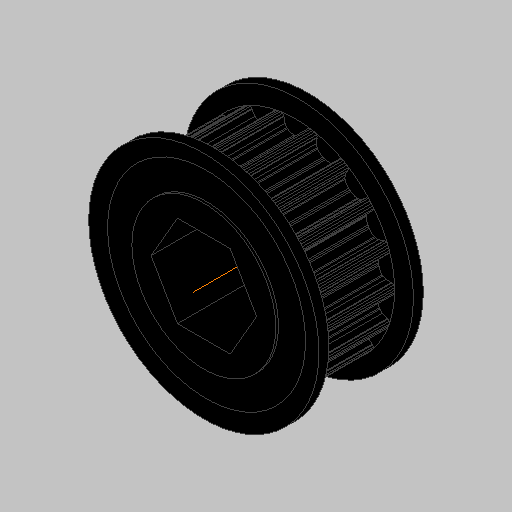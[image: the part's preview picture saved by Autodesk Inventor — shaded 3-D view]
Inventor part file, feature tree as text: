
AUTODESK INVENTOR PART (.ipt)
format: ipt  version: 2023.5 (Build 275446000, 446)  size: 594,944 bytes
history: native  units: in
note: dims shown in document units (in); Inventor stores cm internally (conversion verified against a paired STEP export)
features: plane x1, mirror x1
ambient origin geometry x8: Origin, YZ Plane, XZ Plane, XY Plane, X Axis, Y Axis, Z Axis, Center Point
bodies: Solid1 (feature_tree)
feature tree (2):
  plane  "Work Plane1"
  mirror  "Mirror1"
